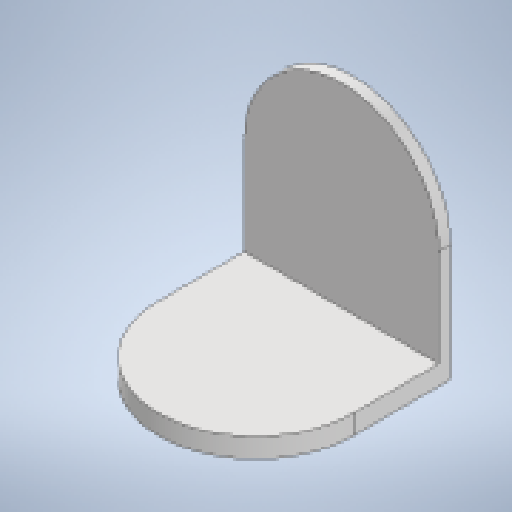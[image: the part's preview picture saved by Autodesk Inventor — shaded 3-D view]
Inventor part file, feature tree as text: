
AUTODESK INVENTOR PART (.ipt)
format: ipt  version: 2023 (Build 270158000, 158)  size: 143,872 bytes
history: native  units: mm
features: extrude x3, sketch x3, other x1, projected_geometry x1
ambient origin geometry x8: Origin, YZ Plane, XZ Plane, XY Plane, X Axis, Y Axis, Z Axis, Center Point
bodies: Body1 (feature_tree)
feature tree (8):
  other  "實體1"
  extrude  "擠出1"  Depth=50.0mm
  extrude  "擠出2"  Depth=3.0mm TaperAngle=0.0deg
  extrude  "擠出3"  Depth=3.0mm
  sketch  "草圖1"
  sketch  "草圖2"
  sketch  "草圖3"
  projected_geometry  "投影迴路1"
